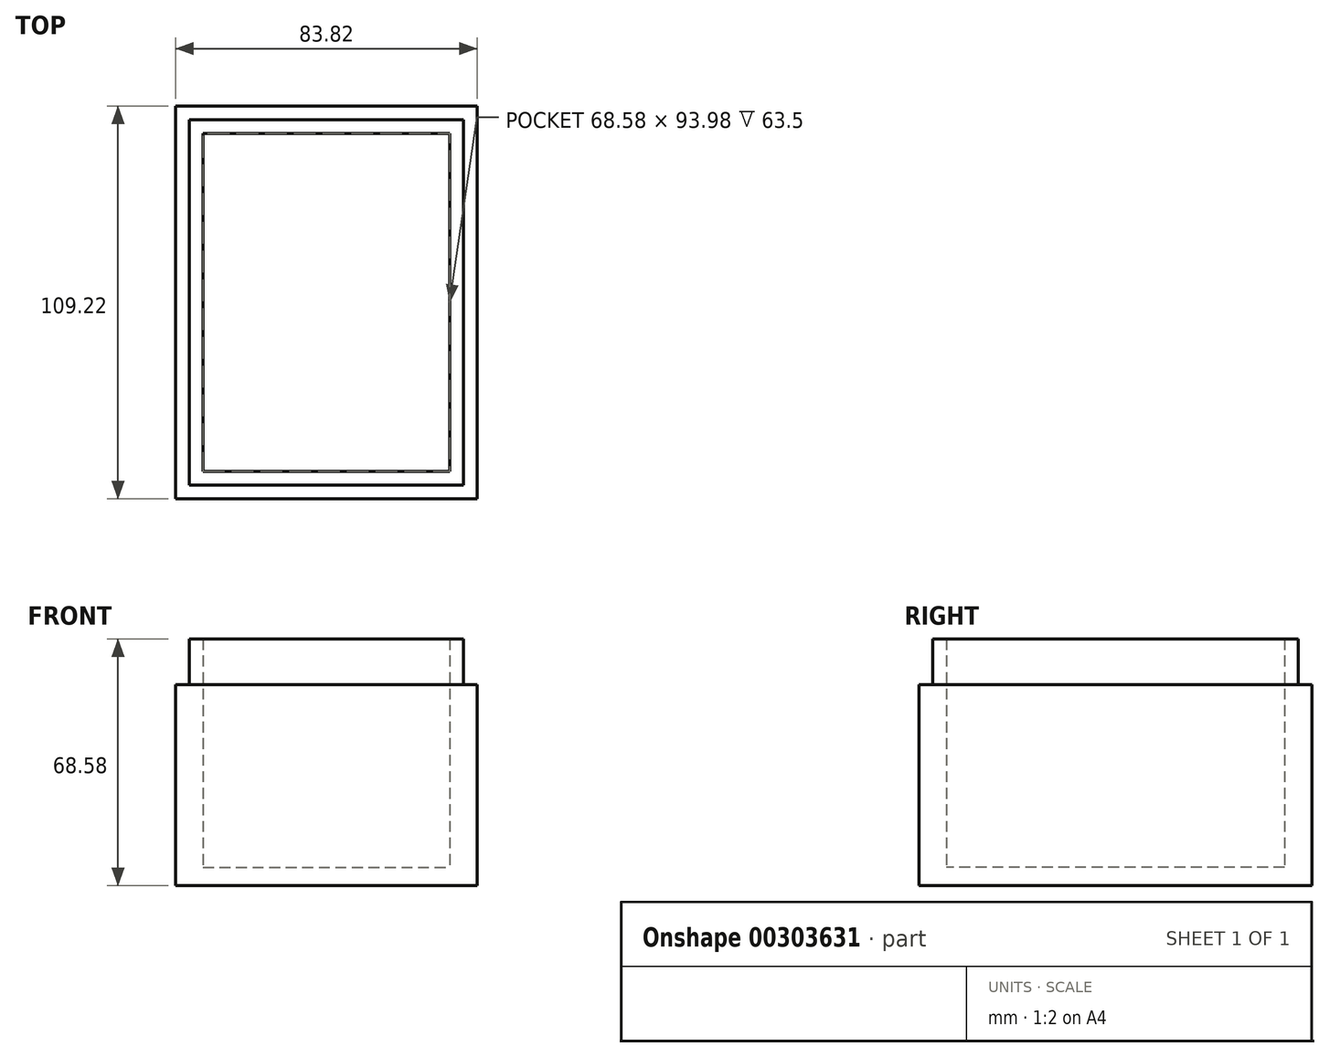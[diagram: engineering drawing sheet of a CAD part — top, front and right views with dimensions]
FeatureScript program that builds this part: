
annotation { "Feature Type Name" : "Feature", "Feature Type Description" : "" }
export const myFeature = defineFeature(function(context is Context, id is Id, definition is map)
    precondition{}
    {
        {
            var Q0;
            Q0=qCreatedBy(makeId("Top.planeOp"),FACE);
            var sketch = newSketch(context, id + "F0", { "sketchPlane" : qUnion([Q0])});
            skLineSegment(sketch, "E0.bottom", {"start": v(41.91, 54.6) * mm, "end": v(-41.9, 54.61) * mm});
            skLineSegment(sketch, "E0.top", {"start": v(41.9, -54.61) * mm, "end": v(-41.91, -54.6) * mm});
            skLineSegment(sketch, "E0.left", {"start": v(41.91, 54.6) * mm, "end": v(41.9, -54.61) * mm});
            skLineSegment(sketch, "E0.right", {"start": v(-41.9, 54.61) * mm, "end": v(-41.9, -54.61) * mm});
            skPoint(sketch, "E0.middle", {"position": v(0, 0) * mm});
            skLineSegment(sketch, "E1.bottom", {"start": v(-34.3, 47) * mm, "end": v(34.3, 47) * mm});
            skLineSegment(sketch, "E1.top", {"start": v(-34.3, -47) * mm, "end": v(34.3, -47) * mm});
            skLineSegment(sketch, "E1.left", {"start": v(-34.3, 47) * mm, "end": v(-34.3, -46.99) * mm});
            skLineSegment(sketch, "E1.right", {"start": v(34.3, 47) * mm, "end": v(34.3, -46.99) * mm});
            skLineSegment(sketch, "E2.bottom", {"start": v(-38.1, 50.8) * mm, "end": v(38.1, 50.8) * mm});
            skLineSegment(sketch, "E2.top", {"start": v(-38.1, -50.8) * mm, "end": v(38.1, -50.8) * mm});
            skLineSegment(sketch, "E2.left", {"start": v(-38.1, 50.8) * mm, "end": v(-38.1, -50.8) * mm});
            skLineSegment(sketch, "E2.right", {"start": v(38.1, 50.8) * mm, "end": v(38.1, -50.8) * mm});
            skSolve(sketch);
        }
        {
            var Q0;
            Q0=makeQuery(id+"F0.imprint","IMPRINT",FACE,{"disambiguationData":[TD([[makeQuery(id+"F0.imprint","IMPRINT",EDGE,{"derivedFrom":sQuery(id+"F0.wireOp",EDGE,"E1.bottom")}),1.0]])]});
            extrude(context, id + "F1", {"entities" : qUnion([Q0]), "depth" : 68.58 * mm});
        }
        {
            var Q0;
            Q0 = qSketchRegion(id + "F0", true);
            extrude(context, id + "F2", {"entities" : qUnion([Q0]), "operationType" : NewBodyOperationType.ADD, "depth" : 55.88 * mm});
        }
        {
            var Q0;
            Q0=qCreatedBy(makeId("Top.planeOp"),FACE);
            var sketch = newSketch(context, id + "F3", { "sketchPlane" : qUnion([Q0])});
            skLineSegment(sketch, "E3.bottom", {"start": v(-34.29, 47) * mm, "end": v(34.3, 47) * mm});
            skLineSegment(sketch, "E3.top", {"start": v(-34.3, -46.99) * mm, "end": v(34.3, -46.99) * mm});
            skLineSegment(sketch, "E3.left", {"start": v(-34.29, 47) * mm, "end": v(-34.3, -46.99) * mm});
            skLineSegment(sketch, "E3.right", {"start": v(34.3, 47) * mm, "end": v(34.3, -46.99) * mm});
            skPoint(sketch, "E3.middle", {"position": v(0, 0) * mm});
            skSolve(sketch);
        }
        {
            var Q0;
            Q0 = qSketchRegion(id + "F3", true);
            extrude(context, id + "F4", {"entities" : qUnion([Q0]), "operationType" : NewBodyOperationType.ADD, "depth" : 5.08 * mm});
        }
    });
